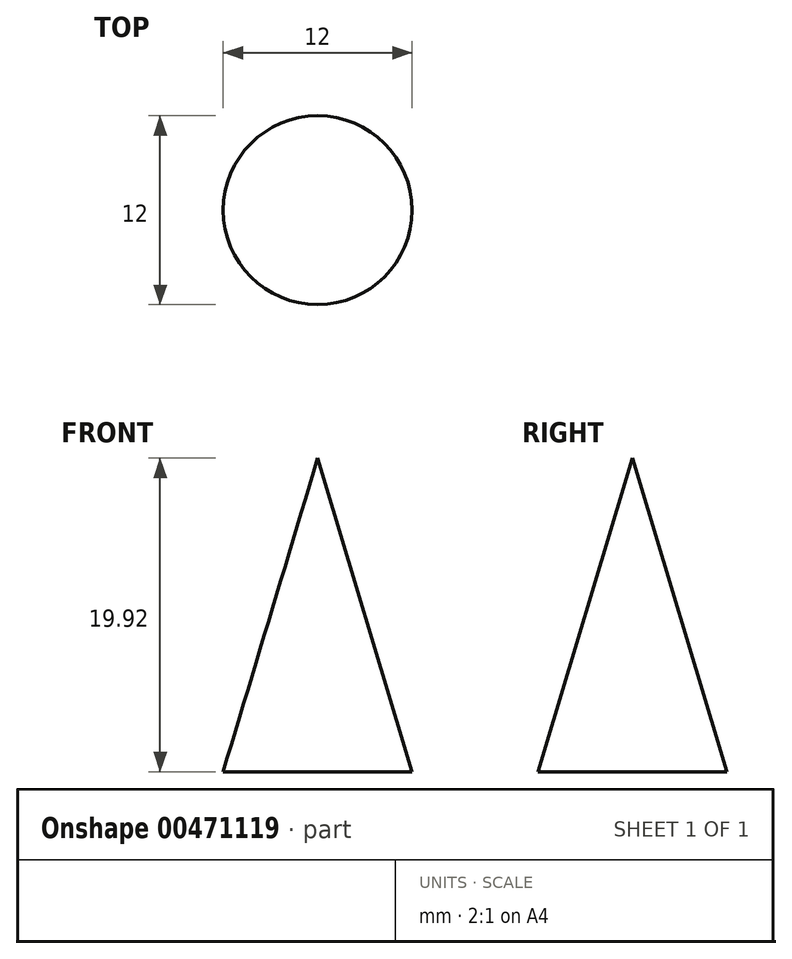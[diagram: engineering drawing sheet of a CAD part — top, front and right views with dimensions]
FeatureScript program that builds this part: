
annotation { "Feature Type Name" : "Feature", "Feature Type Description" : "" }
export const myFeature = defineFeature(function(context is Context, id is Id, definition is map)
    precondition{}
    {
        {
            var Q0;
            Q0=qCreatedBy(makeId("Front.planeOp"),FACE);
            var sketch = newSketch(context, id + "F0", { "sketchPlane" : qUnion([Q0])});
            skLineSegment(sketch, "E0", {"start": v(0, 63.86) * mm, "end": v(0, -48.3) * mm, "construction": true});
            skSolve(sketch);
        }
        {
            var Q0;
            Q0=qCreatedBy(makeId("Front.planeOp"),FACE);
            var sketch = newSketch(context, id + "F1", { "sketchPlane" : qUnion([Q0])});
            skLineSegment(sketch, "E1", {"start": v(0, 0) * mm, "end": v(-6, 0) * mm});
            skLineSegment(sketch, "E2", {"start": v(-6, 0) * mm, "end": v(0, 19.92) * mm});
            skSolve(sketch);
        }
        {
            var Q0;
            Q0=sQuery(id+"F1.wireOp",EDGE,"E2");
            var Q1;
            Q1=sQuery(id+"F1.wireOp",EDGE,"E1");
            var Q2;
            Q2=sQuery(id+"F0.wireOp",EDGE,"E0");
            revolve(context, id + "F2", {"bodyType" : ToolBodyType.SURFACE, "surfaceEntities" : qUnion([Q0, Q1]), "axis" : qUnion([Q2]), "revolveType" : RevolveType.FULL});
        }
    });
